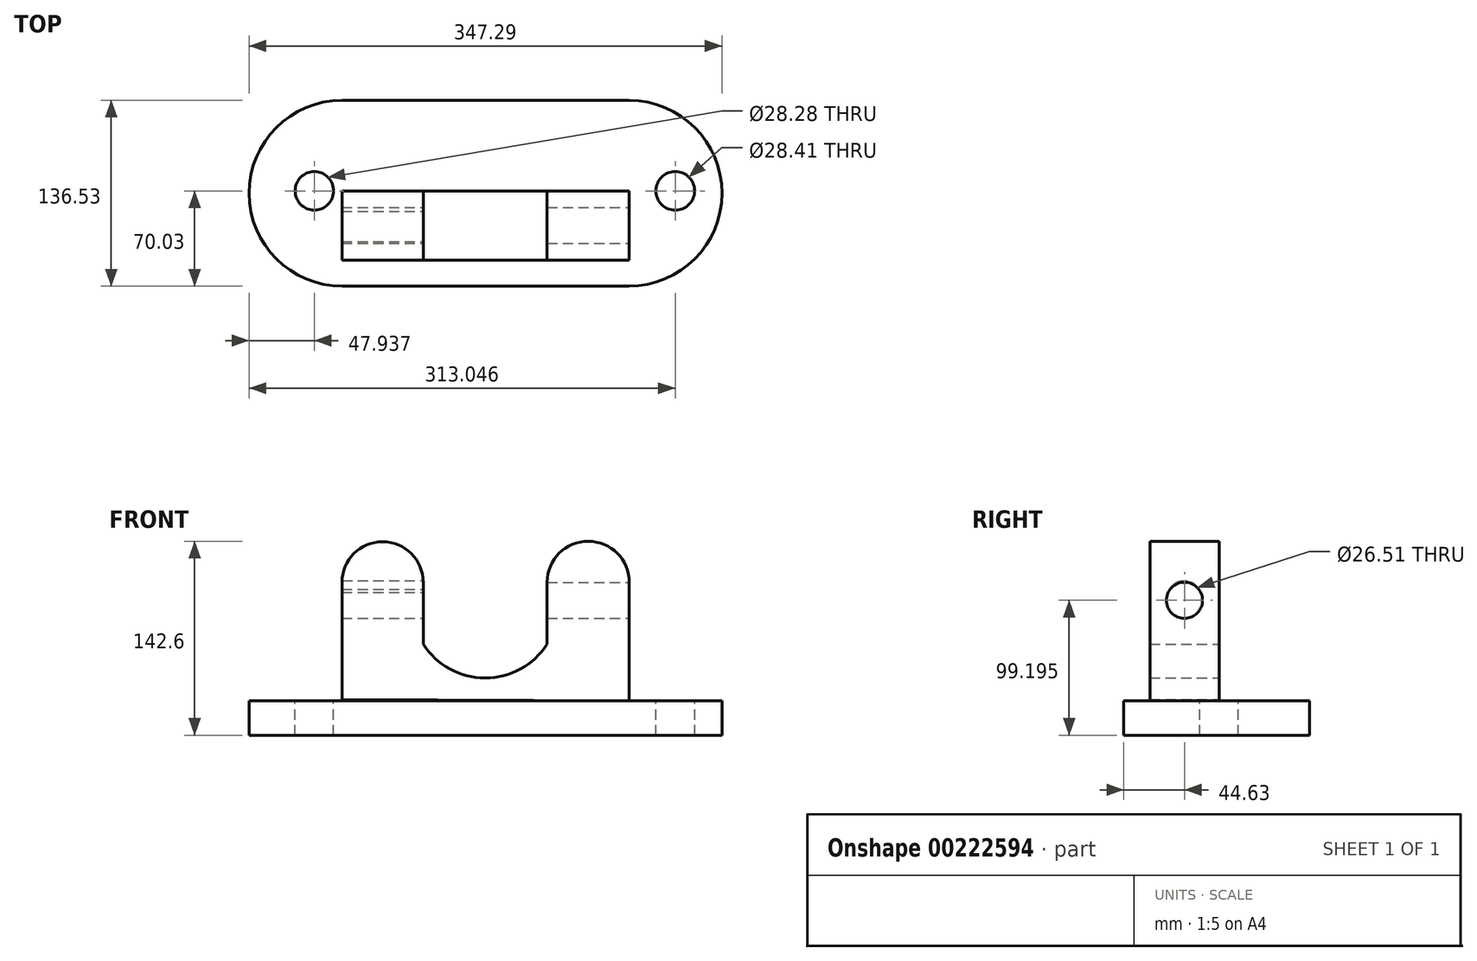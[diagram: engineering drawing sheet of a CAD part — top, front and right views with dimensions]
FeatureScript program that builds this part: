
annotation { "Feature Type Name" : "Feature", "Feature Type Description" : "" }
export const myFeature = defineFeature(function(context is Context, id is Id, definition is map)
    precondition{}
    {
        {
            var Q0;
            Q0=qCreatedBy(makeId("Top.planeOp"),FACE);
            var sketch = newSketch(context, id + "F0", { "sketchPlane" : qUnion([Q0])});
            skLineSegment(sketch, "E0", {"start": v(-76, 66.5) * mm, "end": v(134.76, 66.5) * mm});
            skLineSegment(sketch, "E1", {"start": v(-76, -70.03) * mm, "end": v(134.76, -70.03) * mm});
            skArc(sketch, "E2", {"start": v(-76, 66.5) * mm, "mid": v(-144.26, -1.77) * mm, "end": v(-76, -70.03) * mm});
            skArc(sketch, "E3", {"start": v(134.76, -70.03) * mm, "mid": v(203.03, -1.77) * mm, "end": v(134.76, 66.5) * mm});
            skSolve(sketch);
        }
        {
            var Q0;
            Q0 = qSketchRegion(id + "F0", true);
            extrude(context, id + "F1", {"entities" : qUnion([Q0]), "depth" : 25.4 * mm});
        }
        {
            var Q0;
            Q0=makeQuery(id+"F1.opExtrude","CAP_FACE",FACE,{"disambiguationData":[OSD([sQuery(id+"F0.wireOp",EDGE,"E0"),sQuery(id+"F0.wireOp",EDGE,"E1"),sQuery(id+"F0.wireOp",EDGE,"E2"),sQuery(id+"F0.wireOp",EDGE,"E3")])],"isStart":false});
            var sketch = newSketch(context, id + "F2", { "sketchPlane" : qUnion([Q0])});
            skCircle(sketch, "E4", {"center": v(-96.32, 0) * mm, "radius": 14.14 * mm});
            skSolve(sketch);
        }
        {
            var Q0;
            Q0 = qSketchRegion(id + "F2", true);
            extrude(context, id + "F3", {"entities" : qUnion([Q0]), "operationType" : NewBodyOperationType.REMOVE, "endBound" : BoundingType.THROUGH_ALL, "oppositeDirection" : true, "depth" : 25.4 * mm});
        }
        {
            var Q0;
            Q0=makeQuery(id+"F1.opExtrude","CAP_FACE",FACE,{"disambiguationData":[OSD([sQuery(id+"F0.wireOp",EDGE,"E0"),sQuery(id+"F0.wireOp",EDGE,"E1"),sQuery(id+"F0.wireOp",EDGE,"E2"),sQuery(id+"F0.wireOp",EDGE,"E3")])],"isStart":false});
            var sketch = newSketch(context, id + "F4", { "sketchPlane" : qUnion([Q0])});
            skCircle(sketch, "E5", {"center": v(168.79, 0) * mm, "radius": 14.2 * mm});
            skSolve(sketch);
        }
        {
            var Q0;
            Q0 = qSketchRegion(id + "F4", true);
            extrude(context, id + "F5", {"entities" : qUnion([Q0]), "operationType" : NewBodyOperationType.REMOVE, "endBound" : BoundingType.THROUGH_ALL, "oppositeDirection" : true, "depth" : 25.4 * mm});
        }
        {
            var Q0;
            Q0=qCreatedBy(makeId("Front.planeOp"),FACE);
            var sketch = newSketch(context, id + "F6", { "sketchPlane" : qUnion([Q0])});
            skLineSegment(sketch, "E6", {"start": v(-76, 26.29) * mm, "end": v(-76, 76.22) * mm});
            skLineSegment(sketch, "E7", {"start": v(134.76, 25.4) * mm, "end": v(-76, 26.29) * mm});
            skLineSegment(sketch, "E8", {"start": v(134.76, 25.4) * mm, "end": v(134.98, 76.22) * mm});
            skLineSegment(sketch, "E9", {"start": v(134.98, 76.22) * mm, "end": v(134.98, 112.45) * mm});
            skLineSegment(sketch, "E10", {"start": v(-76, 76.22) * mm, "end": v(-76, 112.45) * mm});
            skLineSegment(sketch, "E11", {"start": v(-16.35, 112.45) * mm, "end": v(-16.35, 66.94) * mm});
            skLineSegment(sketch, "E12", {"start": v(74.67, 112.45) * mm, "end": v(74.67, 66.94) * mm});
            skArc(sketch, "E13", {"start": v(-16.35, 66.94) * mm, "mid": v(29.16, 42.05) * mm, "end": v(74.67, 66.94) * mm});
            skArc(sketch, "E14", {"start": v(134.98, 112.45) * mm, "mid": v(104.82, 142.6) * mm, "end": v(74.67, 112.45) * mm});
            skArc(sketch, "E15", {"start": v(-16.35, 112.45) * mm, "mid": v(-46.17, 142.28) * mm, "end": v(-76, 112.45) * mm});
            skSolve(sketch);
        }
        {
            var Q0;
            Q0 = qSketchRegion(id + "F6", true);
            extrude(context, id + "F7", {"entities" : qUnion([Q0]), "depth" : 50.8 * mm});
        }
        {
            var Q0;
            Q0=qCreatedBy(makeId("Right.planeOp"),FACE);
            var sketch = newSketch(context, id + "F8", { "sketchPlane" : qUnion([Q0])});
            skCircle(sketch, "E16", {"center": v(-25.63, 101.4) * mm, "radius": 12.22 * mm});
            skSolve(sketch);
        }
        {
            var Q0;
            Q0 = qSketchRegion(id + "F8", true);
            extrude(context, id + "F9", {"entities" : qUnion([Q0]), "operationType" : NewBodyOperationType.REMOVE, "endBound" : BoundingType.THROUGH_ALL, "oppositeDirection" : true, "depth" : 25.4 * mm});
        }
        {
            var Q0;
            Q0=makeQuery(id+"F7.opExtrude","SWEPT_FACE",FACE,{"disambiguationData":[OSD([sQuery(id+"F6.wireOp",EDGE,"E9")])]});
            var sketch = newSketch(context, id + "F10", { "sketchPlane" : qUnion([Q0])});
            skCircle(sketch, "E17", {"center": v(-25.4, 99.2) * mm, "radius": 13.26 * mm});
            skPoint(sketch, "E17.centerSnap0", {"position": v(-25.4, 112.45) * mm});
            skSolve(sketch);
        }
        {
            var Q0;
            Q0=makeQuery(id+"F10.imprint","IMPRINT",FACE,{"disambiguationData":[TD([[makeQuery(id+"F10.imprint","IMPRINT",EDGE,{"derivedFrom":sQuery(id+"F10.wireOp",EDGE,"E17")}),1.0]])]});
            extrude(context, id + "F11", {"entities" : qUnion([Q0]), "operationType" : NewBodyOperationType.REMOVE, "endBound" : BoundingType.THROUGH_ALL, "oppositeDirection" : true, "depth" : 25.4 * mm});
        }
    });
